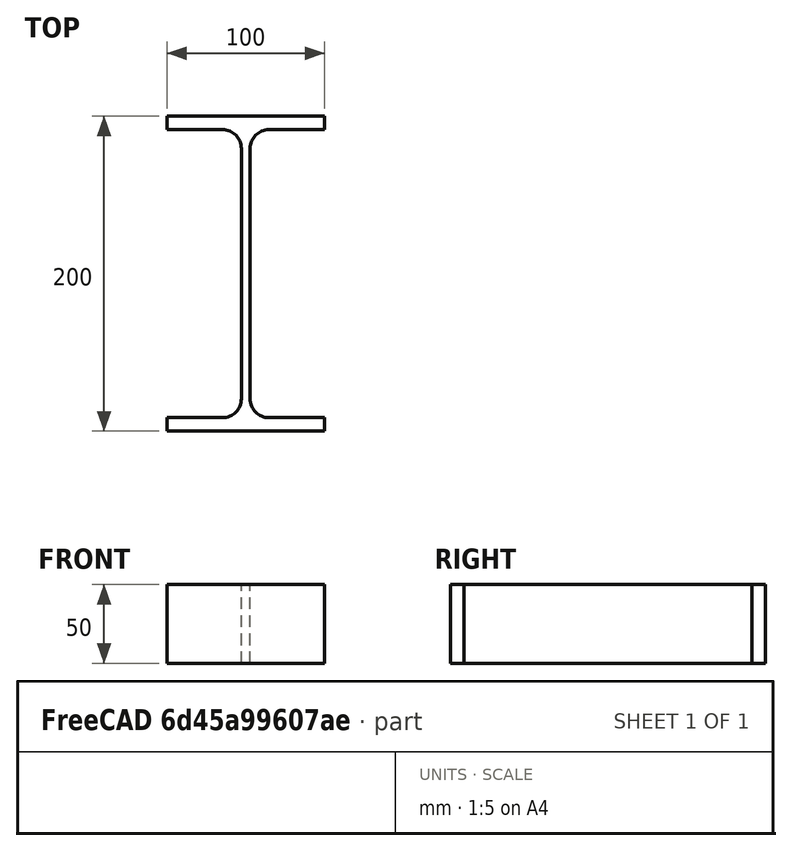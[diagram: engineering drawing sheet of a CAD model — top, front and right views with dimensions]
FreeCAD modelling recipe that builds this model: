
FCSTD DOCUMENT  (FreeCAD 0.15R4671 (Git))
Label: IPE-Profile 200 DIN1025-5 S235JR
License: All rights reserved
LicenseURL: http://en.wikipedia.org/wiki/All_rights_reserved
objects: Sketcher::SketchObject×1, Part::Extrusion×1
note: 2 computed .brp shape members not serialized (recipe doc carries the construction recipe); baked Part::Feature solids carry a one-line shape summary decoded from their .brp

FEATURE [Sketcher::SketchObject] Sketch
  sketch-geometry (16):
    g0: LineSegment StartX=2.8 StartY=-79.5 StartZ=0 EndX=2.8 EndY=79.5 EndZ=0
    g1: LineSegment StartX=14.8 StartY=91.5 StartZ=0 EndX=50 EndY=91.5 EndZ=0
    g2: LineSegment StartX=50 StartY=91.5 StartZ=0 EndX=50 EndY=100 EndZ=0
    g3: LineSegment StartX=50 StartY=100 StartZ=0 EndX=-50 EndY=100 EndZ=0
    g4: LineSegment StartX=-50 StartY=100 StartZ=0 EndX=-50 EndY=91.5 EndZ=0
    g5: LineSegment StartX=-50 StartY=91.5 StartZ=0 EndX=-14.8 EndY=91.5 EndZ=0
    g6: LineSegment StartX=-2.8 StartY=79.5 StartZ=0 EndX=-2.8 EndY=-79.5 EndZ=0
    g7: LineSegment StartX=-14.8 StartY=-91.5 StartZ=0 EndX=-50 EndY=-91.5 EndZ=0
    g8: LineSegment StartX=-50 StartY=-91.5 StartZ=0 EndX=-50 EndY=-100 EndZ=0
    g9: LineSegment StartX=-50 StartY=-100 StartZ=0 EndX=50 EndY=-100 EndZ=0
    g10: LineSegment StartX=50 StartY=-100 StartZ=0 EndX=50 EndY=-91.5 EndZ=0
    g11: LineSegment StartX=50 StartY=-91.5 StartZ=0 EndX=14.8 EndY=-91.5 EndZ=0
    g12: ArcOfCircle CenterX=14.8 CenterY=79.5 CenterZ=0 NormalX=0 NormalY=0 NormalZ=1 Radius=12 StartAngle=1.5708 EndAngle=3.14159
    g13: ArcOfCircle CenterX=14.8 CenterY=-79.5 CenterZ=0 NormalX=0 NormalY=0 NormalZ=1 Radius=12 StartAngle=3.14159 EndAngle=4.71239
    g14: ArcOfCircle CenterX=-14.8 CenterY=79.5 CenterZ=0 NormalX=0 NormalY=0 NormalZ=1 Radius=12 StartAngle=0 EndAngle=1.5708
    g15: ArcOfCircle CenterX=-14.8 CenterY=-79.5 CenterZ=0 NormalX=0 NormalY=0 NormalZ=1 Radius=12 StartAngle=4.71239 EndAngle=6.28319
  constraints (42):
    c: Vertical(g0)
    c: Coincident(g2,g1)
    c: Vertical(g2)
    c: Coincident(g3,g2)
    c: Coincident(g4,g3)
    c: Vertical(g4)
    c: Coincident(g5,g4)
    c: Horizontal(g5)
    c: Vertical(g6)
    c: Horizontal(g7)
    c: Coincident(g8,g7)
    c: Vertical(g8)
    c: Coincident(g9,g8)
    c: Horizontal(g9)
    c: Coincident(g10,g9)
    c: Vertical(g10)
    c: Coincident(g11,g10)
    c: Horizontal(g11)
    c: Tangent(g1,g12) = 1.5708
    c: Tangent(g0,g12) = 1.5708
    c: Tangent(g0,g13) = 1.5708
    c: Tangent(g11,g13) = 1.5708
    c: Tangent(g5,g14) = 1.5708
    c: Tangent(g6,g14) = 1.5708
    c: Tangent(g6,g15) = 1.5708
    c: Tangent(g7,g15) = 1.5708
    c: Equal(g3,g9)
    c: Equal(g2,g4)
    c: Equal(g4,g8)
    c: Equal(g8,g10)
    c: Equal(g12,g14)
    c: Equal(g14,g15)
    c: Equal(g15,g13)
    c: Symmetric(g2,g3,g-2)
    c: Symmetric(g9,g8,g-2)
    c: Symmetric(g0,g6,g-2)
    c: Symmetric(g2,g9,g-1)
    c: DistanceY(g2,g9) = -200
    c: DistanceX(g3) = -100
    c: DistanceX(g0,g6) = -5.6
    c: DistanceY(g2) = 8.5
    c: Radius(g12) = 12
FEATURE [Part::Extrusion] Extrude  label="IPE-Profile 200 DIN1025-5 S235JR"
  Base = -> Sketch
  Dir = (0,0,50)
  Solid = true
